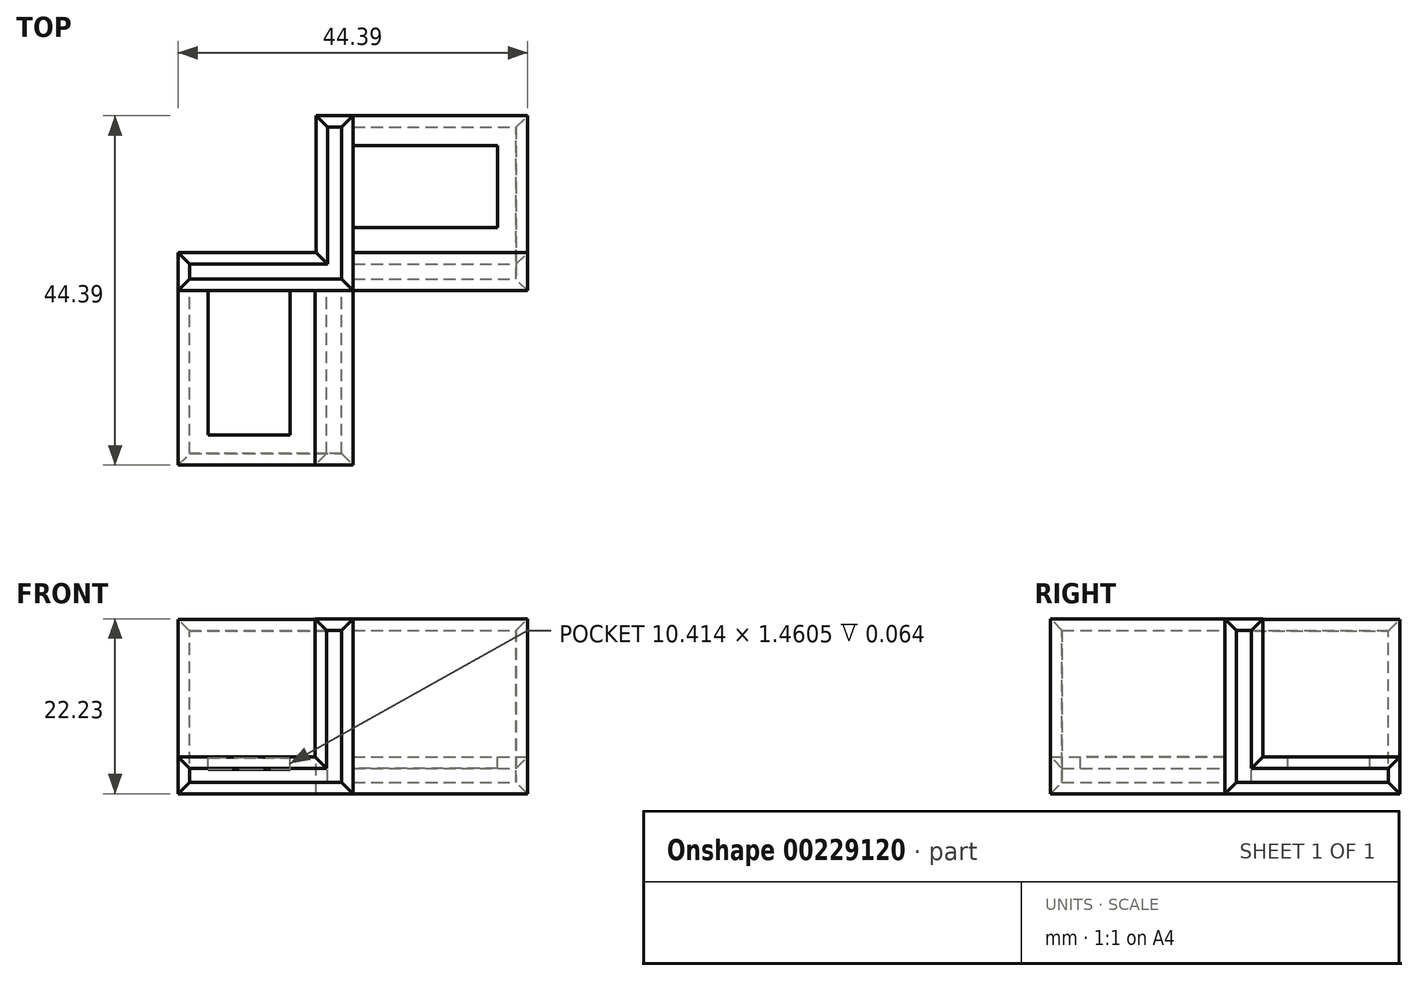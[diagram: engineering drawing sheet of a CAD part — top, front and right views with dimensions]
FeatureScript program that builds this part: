
annotation { "Feature Type Name" : "Feature", "Feature Type Description" : "" }
export const myFeature = defineFeature(function(context is Context, id is Id, definition is map)
    precondition{}
    {
        {
            var Q0;
            Q0=qCreatedBy(makeId("Front.planeOp"),FACE);
            var sketch = newSketch(context, id + "F0", { "sketchPlane" : qUnion([Q0])});
            skLineSegment(sketch, "E0.bottom", {"start": v(0, 19.05) * mm, "end": v(1.78, 19.05) * mm});
            skLineSegment(sketch, "E0.left", {"start": v(0, 19.05) * mm, "end": v(0, -0.25) * mm});
            skLineSegment(sketch, "E0.right", {"start": v(1.78, 19.05) * mm, "end": v(1.78, 1.65) * mm});
            skLineSegment(sketch, "E1.bottom", {"start": v(1.78, 1.65) * mm, "end": v(19.3, 1.65) * mm});
            skLineSegment(sketch, "E1.top", {"start": v(0, -0.25) * mm, "end": v(19.3, -0.25) * mm});
            skLineSegment(sketch, "E1.right", {"start": v(19.3, 1.65) * mm, "end": v(19.3, -0.25) * mm});
            skLineSegment(sketch, "E2.0", {"start": v(-1.46, 20.51) * mm, "end": v(3.24, 20.51) * mm});
            skLineSegment(sketch, "E2.1", {"start": v(-1.46, -1.71) * mm, "end": v(20.76, -1.71) * mm});
            skLineSegment(sketch, "E2.2", {"start": v(20.76, 3.11) * mm, "end": v(20.76, -1.71) * mm});
            skLineSegment(sketch, "E2.3", {"start": v(-1.46, 20.51) * mm, "end": v(-1.46, -1.71) * mm});
            skLineSegment(sketch, "E2.4", {"start": v(3.24, 3.11) * mm, "end": v(20.76, 3.11) * mm});
            skLineSegment(sketch, "E2.5", {"start": v(3.24, 20.51) * mm, "end": v(3.24, 3.11) * mm});
            skSolve(sketch);
        }
        {
            var Q0;
            Q0=makeQuery(id+"F0.imprint","IMPRINT",FACE,{"disambiguationData":[TD([[makeQuery(id+"F0.imprint","IMPRINT",EDGE,{"derivedFrom":sQuery(id+"F0.wireOp",EDGE,"E0.bottom")}),1.0]])]});
            extrude(context, id + "F1", {"entities" : qUnion([Q0]), "depth" : 22.16 * mm});
        }
        {
            var Q0;
            Q0=makeQuery(id+"F1.opExtrude","SWEPT_BODY",BODY,{"disambiguationData":[OSD([sQuery(id+"F0.wireOp",EDGE,"E0.bottom"),sQuery(id+"F0.wireOp",EDGE,"E0.left"),sQuery(id+"F0.wireOp",EDGE,"E0.right"),sQuery(id+"F0.wireOp",EDGE,"E1.bottom"),sQuery(id+"F0.wireOp",EDGE,"E1.top"),sQuery(id+"F0.wireOp",EDGE,"E1.right"),sQuery(id+"F0.wireOp",EDGE,"E2.0"),sQuery(id+"F0.wireOp",EDGE,"E2.1"),sQuery(id+"F0.wireOp",EDGE,"E2.2"),sQuery(id+"F0.wireOp",EDGE,"E2.3"),sQuery(id+"F0.wireOp",EDGE,"E2.4"),sQuery(id+"F0.wireOp",EDGE,"E2.5")])]});
            var Q1;
            Q1=makeQuery(id+"F1.opExtrude","CAP_EDGE",EDGE,{"disambiguationData":[OSD([sQuery(id+"F0.wireOp",EDGE,"E2.4")])],"isStart":true});
            transform(context, id + "F2", {"entities" : qUnion([Q0]), "transformType" : TransformType.ROTATION, "transformAxis" : qUnion([Q1]), "angle" : 90 * degree, "makeCopy" : true});
        }
        {
            var Q0;
            Q0=makeQuery(id+"F2.opPattern","COPY",BODY,{"derivedFrom":makeQuery(id+"F1.opExtrude","SWEPT_BODY",BODY,{"disambiguationData":[OSD([sQuery(id+"F0.wireOp",EDGE,"E0.bottom"),sQuery(id+"F0.wireOp",EDGE,"E0.left"),sQuery(id+"F0.wireOp",EDGE,"E0.right"),sQuery(id+"F0.wireOp",EDGE,"E1.bottom"),sQuery(id+"F0.wireOp",EDGE,"E1.top"),sQuery(id+"F0.wireOp",EDGE,"E1.right"),sQuery(id+"F0.wireOp",EDGE,"E2.0"),sQuery(id+"F0.wireOp",EDGE,"E2.1"),sQuery(id+"F0.wireOp",EDGE,"E2.2"),sQuery(id+"F0.wireOp",EDGE,"E2.3"),sQuery(id+"F0.wireOp",EDGE,"E2.4"),sQuery(id+"F0.wireOp",EDGE,"E2.5")])]}),"instanceName":"1"});
            var Q1;
            Q1=makeQuery(id+"F2.opPattern","COPY",EDGE,{"derivedFrom":makeQuery(id+"F1.opExtrude","SWEPT_EDGE",EDGE,{"disambiguationData":[OSD([sQuery(id+"F0.wireOp",EDGE,"E2.2"),sQuery(id+"F0.wireOp",EDGE,"E2.4")])]}),"instanceName":"1"});
            transform(context, id + "F3", {"entities" : qUnion([Q0]), "transformType" : TransformType.ROTATION, "transformAxis" : qUnion([Q1]), "angle" : 180 * degree, "oppositeDirection" : true, "makeCopy" : false});
        }
        {
            var Q0;
            Q0=makeQuery(id+"F2.opPattern","COPY",BODY,{"derivedFrom":makeQuery(id+"F1.opExtrude","SWEPT_BODY",BODY,{"disambiguationData":[OSD([sQuery(id+"F0.wireOp",EDGE,"E0.bottom"),sQuery(id+"F0.wireOp",EDGE,"E0.left"),sQuery(id+"F0.wireOp",EDGE,"E0.right"),sQuery(id+"F0.wireOp",EDGE,"E1.bottom"),sQuery(id+"F0.wireOp",EDGE,"E1.top"),sQuery(id+"F0.wireOp",EDGE,"E1.right"),sQuery(id+"F0.wireOp",EDGE,"E2.0"),sQuery(id+"F0.wireOp",EDGE,"E2.1"),sQuery(id+"F0.wireOp",EDGE,"E2.2"),sQuery(id+"F0.wireOp",EDGE,"E2.3"),sQuery(id+"F0.wireOp",EDGE,"E2.4"),sQuery(id+"F0.wireOp",EDGE,"E2.5")])]}),"instanceName":"1"});
            transform(context, id + "F4", {"entities" : qUnion([Q0]), "transformType" : TransformType.TRANSLATION_3D, "dx" : -22.22 * mm, "dy" : 4.76 * mm, "dz" : 17.46 * mm, "makeCopy" : false});
        }
        {
            var Q0;
            Q0=makeQuery(id+"F1.opExtrude","SWEPT_BODY",BODY,{"disambiguationData":[OSD([sQuery(id+"F0.wireOp",EDGE,"E0.bottom"),sQuery(id+"F0.wireOp",EDGE,"E0.left"),sQuery(id+"F0.wireOp",EDGE,"E0.right"),sQuery(id+"F0.wireOp",EDGE,"E1.bottom"),sQuery(id+"F0.wireOp",EDGE,"E1.top"),sQuery(id+"F0.wireOp",EDGE,"E1.right"),sQuery(id+"F0.wireOp",EDGE,"E2.0"),sQuery(id+"F0.wireOp",EDGE,"E2.1"),sQuery(id+"F0.wireOp",EDGE,"E2.2"),sQuery(id+"F0.wireOp",EDGE,"E2.3"),sQuery(id+"F0.wireOp",EDGE,"E2.4"),sQuery(id+"F0.wireOp",EDGE,"E2.5")])]});
            var Q1;
            Q1=makeQuery(id+"F1.opExtrude","SWEPT_EDGE",EDGE,{"disambiguationData":[OSD([sQuery(id+"F0.wireOp",EDGE,"E2.1"),sQuery(id+"F0.wireOp",EDGE,"E2.3")])]});
            transform(context, id + "F5", {"entities" : qUnion([Q0]), "transformType" : TransformType.ROTATION, "transformAxis" : qUnion([Q1]), "angle" : 90 * degree, "oppositeDirection" : true, "makeCopy" : false});
        }
        {
            var Q0;
            Q0=makeQuery(id+"F1.opExtrude","SWEPT_BODY",BODY,{"disambiguationData":[OSD([sQuery(id+"F0.wireOp",EDGE,"E0.bottom"),sQuery(id+"F0.wireOp",EDGE,"E0.left"),sQuery(id+"F0.wireOp",EDGE,"E0.right"),sQuery(id+"F0.wireOp",EDGE,"E1.bottom"),sQuery(id+"F0.wireOp",EDGE,"E1.top"),sQuery(id+"F0.wireOp",EDGE,"E1.right"),sQuery(id+"F0.wireOp",EDGE,"E2.0"),sQuery(id+"F0.wireOp",EDGE,"E2.1"),sQuery(id+"F0.wireOp",EDGE,"E2.2"),sQuery(id+"F0.wireOp",EDGE,"E2.3"),sQuery(id+"F0.wireOp",EDGE,"E2.4"),sQuery(id+"F0.wireOp",EDGE,"E2.5")])]});
            transform(context, id + "F6", {"entities" : qUnion([Q0]), "transformType" : TransformType.TRANSLATION_3D, "dx" : 22.22 * mm, "dy" : 0 * mm, "dz" : 0 * mm, "makeCopy" : false});
        }
        {
            var Q0;
            Q0=makeQuery(id+"F2.opPattern","COPY",BODY,{"derivedFrom":makeQuery(id+"F1.opExtrude","SWEPT_BODY",BODY,{"disambiguationData":[OSD([sQuery(id+"F0.wireOp",EDGE,"E0.bottom"),sQuery(id+"F0.wireOp",EDGE,"E0.left"),sQuery(id+"F0.wireOp",EDGE,"E0.right"),sQuery(id+"F0.wireOp",EDGE,"E1.bottom"),sQuery(id+"F0.wireOp",EDGE,"E1.top"),sQuery(id+"F0.wireOp",EDGE,"E1.right"),sQuery(id+"F0.wireOp",EDGE,"E2.0"),sQuery(id+"F0.wireOp",EDGE,"E2.1"),sQuery(id+"F0.wireOp",EDGE,"E2.2"),sQuery(id+"F0.wireOp",EDGE,"E2.3"),sQuery(id+"F0.wireOp",EDGE,"E2.4"),sQuery(id+"F0.wireOp",EDGE,"E2.5")])]}),"instanceName":"1"});
            var Q1;
            Q1=makeQuery(id+"F2.opPattern","COPY",EDGE,{"derivedFrom":makeQuery(id+"F1.opExtrude","CAP_EDGE",EDGE,{"disambiguationData":[OSD([sQuery(id+"F0.wireOp",EDGE,"E2.3")])],"isStart":false}),"instanceName":"1"});
            transform(context, id + "F7", {"entities" : qUnion([Q0]), "transformType" : TransformType.ROTATION, "transformAxis" : qUnion([Q1]), "angle" : 90 * degree, "oppositeDirection" : true, "makeCopy" : true});
        }
        {
            var Q0;
            Q0=makeQuery(id+"F1.opExtrude","SWEPT_FACE",FACE,{"disambiguationData":[OSD([sQuery(id+"F0.wireOp",EDGE,"E2.5")])]});
            var sketch = newSketch(context, id + "F8", { "sketchPlane" : qUnion([Q0])});
            skPoint(sketch, "E3.centerSnap0", {"position": v(7.24, 0) * mm});
            skPoint(sketch, "E3.centerSnap1", {"position": v(-1.46, -11.08) * mm});
            skLineSegment(sketch, "E4.bottom", {"start": v(2.35, 0) * mm, "end": v(12.76, 0) * mm});
            skLineSegment(sketch, "E4.top", {"start": v(2.35, -18.35) * mm, "end": v(12.76, -18.35) * mm});
            skLineSegment(sketch, "E4.left", {"start": v(2.35, 0) * mm, "end": v(2.35, -18.35) * mm});
            skLineSegment(sketch, "E4.right", {"start": v(12.76, 0) * mm, "end": v(12.76, -18.35) * mm});
            skSolve(sketch);
        }
        {
            var Q0;
            Q0 = qSketchRegion(id + "F8", true);
            extrude(context, id + "F9", {"entities" : qUnion([Q0]), "operationType" : NewBodyOperationType.REMOVE, "endBound" : BoundingType.UP_TO_NEXT, "oppositeDirection" : true, "depth" : 25.4 * mm});
        }
        {
            var Q0;
            Q0=makeQuery(id+"F7.opPattern","COPY",FACE,{"derivedFrom":makeQuery(id+"F2.opPattern","COPY",FACE,{"derivedFrom":makeQuery(id+"F1.opExtrude","SWEPT_FACE",FACE,{"disambiguationData":[OSD([sQuery(id+"F0.wireOp",EDGE,"E2.5")])]}),"instanceName":"1"}),"instanceName":"1"});
            var sketch = newSketch(context, id + "F10", { "sketchPlane" : qUnion([Q0])});
            skPoint(sketch, "E5.centerSnap0", {"position": v(31.85, 4.76) * mm});
            skPoint(sketch, "E5.centerSnap1", {"position": v(20.76, 13.46) * mm});
            skLineSegment(sketch, "E6.bottom", {"start": v(20.76, 18.35) * mm, "end": v(39.12, 18.35) * mm});
            skLineSegment(sketch, "E6.top", {"start": v(20.76, 7.94) * mm, "end": v(39.12, 7.94) * mm});
            skLineSegment(sketch, "E6.left", {"start": v(20.76, 18.35) * mm, "end": v(20.76, 7.94) * mm});
            skLineSegment(sketch, "E6.right", {"start": v(39.12, 18.35) * mm, "end": v(39.12, 7.94) * mm});
            skSolve(sketch);
        }
        {
            var Q0;
            Q0 = qSketchRegion(id + "F10", true);
            extrude(context, id + "F11", {"entities" : qUnion([Q0]), "operationType" : NewBodyOperationType.REMOVE, "endBound" : BoundingType.UP_TO_NEXT, "oppositeDirection" : true, "depth" : 25.4 * mm});
        }
        {
            var Q0;
            Q0=makeQuery(id+"F2.opPattern","COPY",EDGE,{"derivedFrom":makeQuery(id+"F1.opExtrude","CAP_EDGE",EDGE,{"disambiguationData":[OSD([sQuery(id+"F0.wireOp",EDGE,"E1.right")])],"isStart":true}),"instanceName":"1"});
            var Q1;
            Q1=makeQuery(id+"F2.opPattern","COPY",EDGE,{"derivedFrom":makeQuery(id+"F1.opExtrude","CAP_EDGE",EDGE,{"disambiguationData":[OSD([sQuery(id+"F0.wireOp",EDGE,"E1.bottom")])],"isStart":true}),"instanceName":"1"});
            var Q2;
            Q2=makeQuery(id+"F2.opPattern","COPY",EDGE,{"derivedFrom":makeQuery(id+"F1.opExtrude","CAP_EDGE",EDGE,{"disambiguationData":[OSD([sQuery(id+"F0.wireOp",EDGE,"E1.top")])],"isStart":true}),"instanceName":"1"});
            var Q3;
            Q3=makeQuery(id+"F2.opPattern","COPY",EDGE,{"derivedFrom":makeQuery(id+"F1.opExtrude","CAP_EDGE",EDGE,{"disambiguationData":[OSD([sQuery(id+"F0.wireOp",EDGE,"E0.right")])],"isStart":true}),"instanceName":"1"});
            var Q4;
            Q4=makeQuery(id+"F2.opPattern","COPY",EDGE,{"derivedFrom":makeQuery(id+"F1.opExtrude","CAP_EDGE",EDGE,{"disambiguationData":[OSD([sQuery(id+"F0.wireOp",EDGE,"E0.bottom")])],"isStart":true}),"instanceName":"1"});
            var Q5;
            Q5=makeQuery(id+"F2.opPattern","COPY",EDGE,{"derivedFrom":makeQuery(id+"F1.opExtrude","CAP_EDGE",EDGE,{"disambiguationData":[OSD([sQuery(id+"F0.wireOp",EDGE,"E0.left")])],"isStart":true}),"instanceName":"1"});
            var Q6;
            Q6=makeQuery(id+"F7.opPattern","COPY",EDGE,{"derivedFrom":makeQuery(id+"F2.opPattern","COPY",EDGE,{"derivedFrom":makeQuery(id+"F1.opExtrude","CAP_EDGE",EDGE,{"disambiguationData":[OSD([sQuery(id+"F0.wireOp",EDGE,"E1.right")])],"isStart":true}),"instanceName":"1"}),"instanceName":"1"});
            var Q7;
            Q7=makeQuery(id+"F7.opPattern","COPY",EDGE,{"derivedFrom":makeQuery(id+"F2.opPattern","COPY",EDGE,{"derivedFrom":makeQuery(id+"F1.opExtrude","CAP_EDGE",EDGE,{"disambiguationData":[OSD([sQuery(id+"F0.wireOp",EDGE,"E1.bottom")])],"isStart":true}),"instanceName":"1"}),"instanceName":"1"});
            var Q8;
            Q8=makeQuery(id+"F7.opPattern","COPY",EDGE,{"derivedFrom":makeQuery(id+"F2.opPattern","COPY",EDGE,{"derivedFrom":makeQuery(id+"F1.opExtrude","CAP_EDGE",EDGE,{"disambiguationData":[OSD([sQuery(id+"F0.wireOp",EDGE,"E1.top")])],"isStart":true}),"instanceName":"1"}),"instanceName":"1"});
            var Q9;
            Q9=makeQuery(id+"F7.opPattern","COPY",EDGE,{"derivedFrom":makeQuery(id+"F2.opPattern","COPY",EDGE,{"derivedFrom":makeQuery(id+"F1.opExtrude","CAP_EDGE",EDGE,{"disambiguationData":[OSD([sQuery(id+"F0.wireOp",EDGE,"E0.left")])],"isStart":true}),"instanceName":"1"}),"instanceName":"1"});
            var Q10;
            Q10=makeQuery(id+"F7.opPattern","COPY",EDGE,{"derivedFrom":makeQuery(id+"F2.opPattern","COPY",EDGE,{"derivedFrom":makeQuery(id+"F1.opExtrude","CAP_EDGE",EDGE,{"disambiguationData":[OSD([sQuery(id+"F0.wireOp",EDGE,"E0.right")])],"isStart":true}),"instanceName":"1"}),"instanceName":"1"});
            var Q11;
            Q11=makeQuery(id+"F7.opPattern","COPY",EDGE,{"derivedFrom":makeQuery(id+"F2.opPattern","COPY",EDGE,{"derivedFrom":makeQuery(id+"F1.opExtrude","CAP_EDGE",EDGE,{"disambiguationData":[OSD([sQuery(id+"F0.wireOp",EDGE,"E0.bottom")])],"isStart":true}),"instanceName":"1"}),"instanceName":"1"});
            var Q12;
            Q12=makeQuery(id+"F1.opExtrude","CAP_EDGE",EDGE,{"disambiguationData":[OSD([sQuery(id+"F0.wireOp",EDGE,"E1.bottom")])],"isStart":false});
            var Q13;
            Q13=makeQuery(id+"F1.opExtrude","CAP_EDGE",EDGE,{"disambiguationData":[OSD([sQuery(id+"F0.wireOp",EDGE,"E1.top")])],"isStart":false});
            var Q14;
            Q14=makeQuery(id+"F1.opExtrude","CAP_EDGE",EDGE,{"disambiguationData":[OSD([sQuery(id+"F0.wireOp",EDGE,"E1.right")])],"isStart":false});
            var Q15;
            Q15=makeQuery(id+"F1.opExtrude","CAP_EDGE",EDGE,{"disambiguationData":[OSD([sQuery(id+"F0.wireOp",EDGE,"E0.left")])],"isStart":false});
            var Q16;
            Q16=makeQuery(id+"F1.opExtrude","CAP_EDGE",EDGE,{"disambiguationData":[OSD([sQuery(id+"F0.wireOp",EDGE,"E0.bottom")])],"isStart":false});
            var Q17;
            Q17=makeQuery(id+"F1.opExtrude","CAP_EDGE",EDGE,{"disambiguationData":[OSD([sQuery(id+"F0.wireOp",EDGE,"E0.right")])],"isStart":false});
            chamfer(context, id + "F12", {"entities" : qUnion([Q0, Q1, Q2, Q3, Q4, Q5, Q6, Q7, Q8, Q9, Q10, Q11, Q12, Q13, Q14, Q15, Q16, Q17]), "width" : 1.46 * mm, "tangentPropagation" : true});
        }
        {
            var Q0;
            Q0=makeQuery(id+"F7.opPattern","COPY",BODY,{"derivedFrom":makeQuery(id+"F2.opPattern","COPY",BODY,{"derivedFrom":makeQuery(id+"F1.opExtrude","SWEPT_BODY",BODY,{"disambiguationData":[OSD([sQuery(id+"F0.wireOp",EDGE,"E0.bottom"),sQuery(id+"F0.wireOp",EDGE,"E0.left"),sQuery(id+"F0.wireOp",EDGE,"E0.right"),sQuery(id+"F0.wireOp",EDGE,"E1.bottom"),sQuery(id+"F0.wireOp",EDGE,"E1.top"),sQuery(id+"F0.wireOp",EDGE,"E1.right"),sQuery(id+"F0.wireOp",EDGE,"E2.0"),sQuery(id+"F0.wireOp",EDGE,"E2.1"),sQuery(id+"F0.wireOp",EDGE,"E2.2"),sQuery(id+"F0.wireOp",EDGE,"E2.3"),sQuery(id+"F0.wireOp",EDGE,"E2.4"),sQuery(id+"F0.wireOp",EDGE,"E2.5")])]}),"instanceName":"1"}),"instanceName":"1"});
            transform(context, id + "F13", {"entities" : qUnion([Q0]), "transformType" : TransformType.TRANSLATION_3D, "dx" : 0 * mm, "dy" : 0 * mm, "dz" : 0 * mm, "makeCopy" : false});
        }
        {
            var Q0;
            Q0=makeQuery(id+"F1.opExtrude","SWEPT_BODY",BODY,{"disambiguationData":[OSD([sQuery(id+"F0.wireOp",EDGE,"E0.bottom"),sQuery(id+"F0.wireOp",EDGE,"E0.left"),sQuery(id+"F0.wireOp",EDGE,"E0.right"),sQuery(id+"F0.wireOp",EDGE,"E1.bottom"),sQuery(id+"F0.wireOp",EDGE,"E1.top"),sQuery(id+"F0.wireOp",EDGE,"E1.right"),sQuery(id+"F0.wireOp",EDGE,"E2.0"),sQuery(id+"F0.wireOp",EDGE,"E2.1"),sQuery(id+"F0.wireOp",EDGE,"E2.2"),sQuery(id+"F0.wireOp",EDGE,"E2.3"),sQuery(id+"F0.wireOp",EDGE,"E2.4"),sQuery(id+"F0.wireOp",EDGE,"E2.5")])]});
            transform(context, id + "F14", {"entities" : qUnion([Q0]), "transformType" : TransformType.TRANSLATION_3D, "dx" : 0 * mm, "dy" : 0.06 * mm, "dz" : 0 * mm, "makeCopy" : false});
        }
        {
            var Q0;
            Q0=makeQuery(id+"F2.opPattern","COPY",FACE,{"derivedFrom":makeQuery(id+"F1.opExtrude","CAP_FACE",FACE,{"disambiguationData":[OSD([sQuery(id+"F0.wireOp",EDGE,"E0.bottom"),sQuery(id+"F0.wireOp",EDGE,"E0.left"),sQuery(id+"F0.wireOp",EDGE,"E0.right"),sQuery(id+"F0.wireOp",EDGE,"E1.bottom"),sQuery(id+"F0.wireOp",EDGE,"E1.top"),sQuery(id+"F0.wireOp",EDGE,"E1.right"),sQuery(id+"F0.wireOp",EDGE,"E2.0"),sQuery(id+"F0.wireOp",EDGE,"E2.1"),sQuery(id+"F0.wireOp",EDGE,"E2.2"),sQuery(id+"F0.wireOp",EDGE,"E2.3"),sQuery(id+"F0.wireOp",EDGE,"E2.4"),sQuery(id+"F0.wireOp",EDGE,"E2.5")])],"isStart":false}),"instanceName":"1"});
            var sketch = newSketch(context, id + "F15", { "sketchPlane" : qUnion([Q0])});
            skLineSegment(sketch, "E7", {"start": v(19.3, -20.7) * mm, "end": v(17.53, -20.7) * mm});
            skLineSegment(sketch, "E8", {"start": v(17.53, -20.7) * mm, "end": v(17.53, -3.3) * mm});
            skLineSegment(sketch, "E9", {"start": v(17.53, -3.3) * mm, "end": v(0, -3.3) * mm});
            skLineSegment(sketch, "E10", {"start": v(0, -3.3) * mm, "end": v(0, -1.4) * mm});
            skLineSegment(sketch, "E11", {"start": v(0, -1.4) * mm, "end": v(19.3, -1.4) * mm});
            skLineSegment(sketch, "E12", {"start": v(19.3, -1.4) * mm, "end": v(19.3, -20.7) * mm});
            skSolve(sketch);
        }
        {
            var Q0;
            Q0 = qSketchRegion(id + "F15", true);
            extrude(context, id + "F16", {"entities" : qUnion([Q0]), "operationType" : NewBodyOperationType.ADD, "oppositeDirection" : true, "depth" : 1.52 * mm});
        }
        {
            var Q0;
            Q0=makeQuery(id+"F1.opExtrude","SWEPT_BODY",BODY,{"disambiguationData":[OSD([sQuery(id+"F0.wireOp",EDGE,"E0.bottom"),sQuery(id+"F0.wireOp",EDGE,"E0.left"),sQuery(id+"F0.wireOp",EDGE,"E0.right"),sQuery(id+"F0.wireOp",EDGE,"E1.bottom"),sQuery(id+"F0.wireOp",EDGE,"E1.top"),sQuery(id+"F0.wireOp",EDGE,"E1.right"),sQuery(id+"F0.wireOp",EDGE,"E2.0"),sQuery(id+"F0.wireOp",EDGE,"E2.1"),sQuery(id+"F0.wireOp",EDGE,"E2.2"),sQuery(id+"F0.wireOp",EDGE,"E2.3"),sQuery(id+"F0.wireOp",EDGE,"E2.4"),sQuery(id+"F0.wireOp",EDGE,"E2.5")])]});
            transform(context, id + "F17", {"entities" : qUnion([Q0]), "transformType" : TransformType.TRANSLATION_3D, "dx" : 0 * mm, "dy" : -0.13 * mm, "dz" : 0.13 * mm, "makeCopy" : false});
        }
    });
